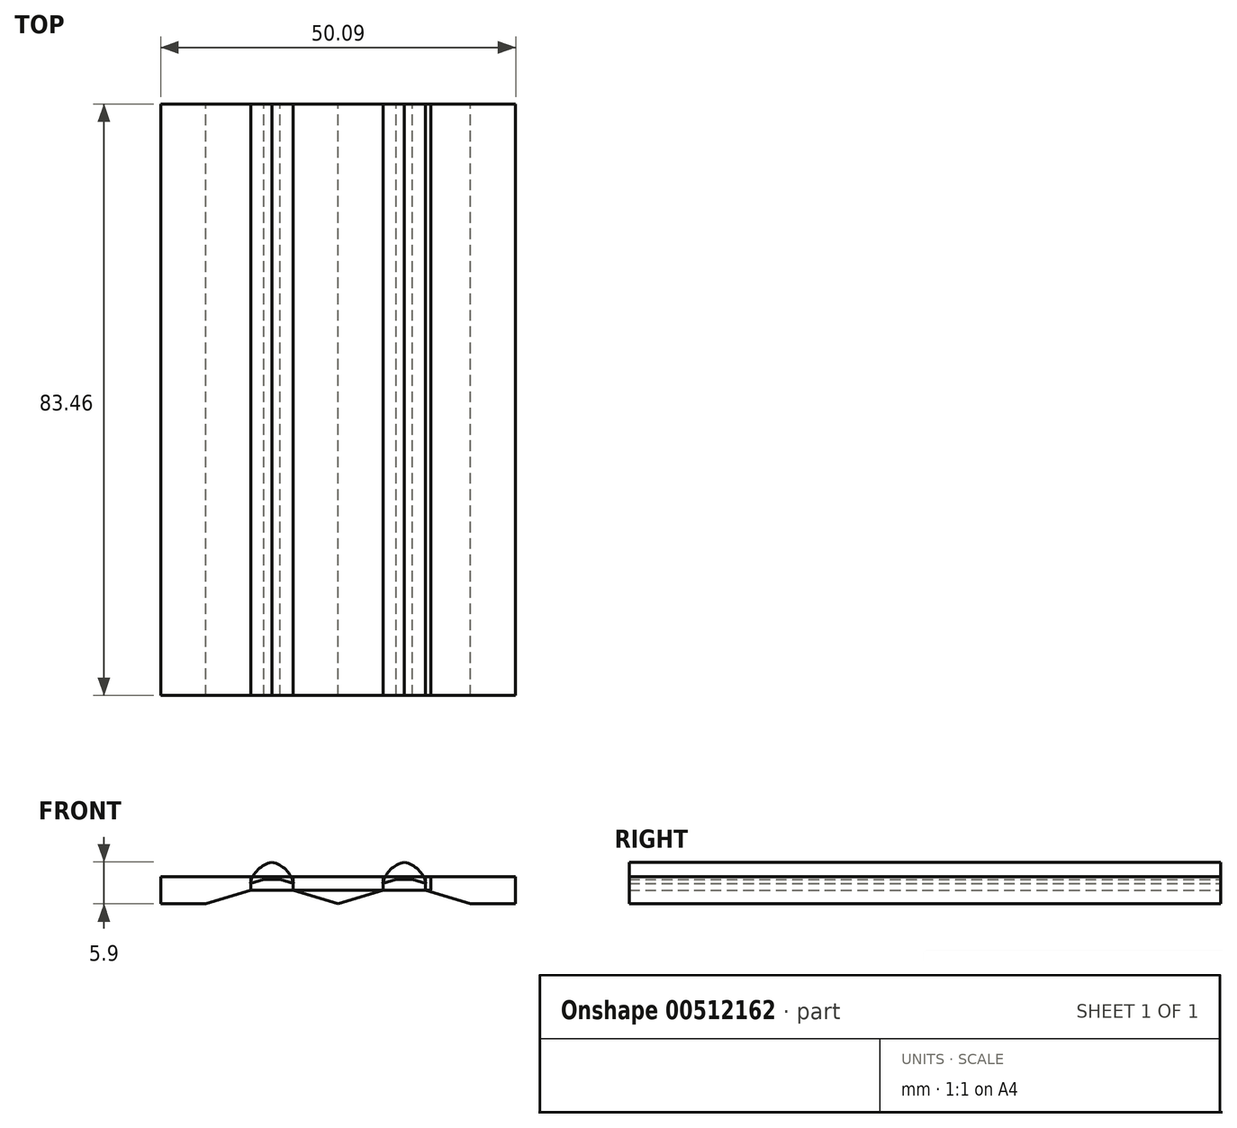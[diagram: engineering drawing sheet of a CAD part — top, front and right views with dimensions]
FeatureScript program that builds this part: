
annotation { "Feature Type Name" : "Feature", "Feature Type Description" : "" }
export const myFeature = defineFeature(function(context is Context, id is Id, definition is map)
    precondition{}
    {
        {
            var Q0;
            Q0=qCreatedBy(makeId("Top.planeOp"),FACE);
            var sketch = newSketch(context, id + "F0", { "sketchPlane" : qUnion([Q0])});
            skLineSegment(sketch, "E0.bottom", {"start": v(-28.3, 40) * mm, "end": v(22.5, 40) * mm});
            skLineSegment(sketch, "E0.top", {"start": v(-28.3, -43.46) * mm, "end": v(22.5, -43.46) * mm});
            skLineSegment(sketch, "E0.left", {"start": v(-28.3, 40) * mm, "end": v(-28.3, -43.46) * mm});
            skLineSegment(sketch, "E0.right", {"start": v(22.5, 40) * mm, "end": v(22.5, -43.46) * mm});
            skLineSegment(sketch, "E1", {"start": v(-15.6, 40) * mm, "end": v(-15.6, -43.46) * mm});
            skLineSegment(sketch, "E2", {"start": v(-15.6, -43.46) * mm, "end": v(-9.26, -43.46) * mm});
            skLineSegment(sketch, "E3", {"start": v(-9.26, -43.46) * mm, "end": v(-9.26, 40) * mm});
            skLineSegment(sketch, "E4", {"start": v(-9.26, 40) * mm, "end": v(3.44, 40) * mm});
            skLineSegment(sketch, "E5", {"start": v(3.44, 40) * mm, "end": v(3.44, -43.46) * mm});
            skLineSegment(sketch, "E6", {"start": v(3.44, -43.46) * mm, "end": v(9.8, -43.46) * mm});
            skLineSegment(sketch, "E7", {"start": v(9.8, -43.46) * mm, "end": v(9.8, 40) * mm});
            skSolve(sketch);
        }
        {
            var Q0;
            {var subQ0=sQuery(id+"F0.wireOp",EDGE,"E0.right");Q0=makeQuery(id+"F0.imprint","IMPRINT",FACE,{"disambiguationData":[TD([[makeQuery(id+"F0.imprint","IMPRINT",EDGE,{"derivedFrom":subQ0}),-1.0]])]});}
            var Q1;
            {var subQ0=sQuery(id+"F0.wireOp",EDGE,"E3");Q1=makeQuery(id+"F0.imprint","IMPRINT",FACE,{"disambiguationData":[TD([[makeQuery(id+"F0.imprint","IMPRINT",EDGE,{"derivedFrom":subQ0}),-1.0]])]});}
            var Q2;
            {var subQ0=sQuery(id+"F0.wireOp",EDGE,"E0.left");Q2=makeQuery(id+"F0.imprint","IMPRINT",FACE,{"disambiguationData":[TD([[makeQuery(id+"F0.imprint","IMPRINT",EDGE,{"derivedFrom":subQ0}),1.0]])]});}
            extrude(context, id + "F1", {"entities" : qUnion([Q0, Q1, Q2]), "depth" : 10.16 * mm});
        }
        {
            var Q0;
            {var subQ0=sQuery(id+"F0.wireOp",EDGE,"E1");Q0=makeQuery(id+"F0.imprint","IMPRINT",FACE,{"disambiguationData":[TD([[makeQuery(id+"F0.imprint","IMPRINT",EDGE,{"derivedFrom":subQ0}),1.0]])]});}
            var Q1;
            {var subQ0=sQuery(id+"F0.wireOp",EDGE,"E5");Q1=makeQuery(id+"F0.imprint","IMPRINT",FACE,{"disambiguationData":[TD([[makeQuery(id+"F0.imprint","IMPRINT",EDGE,{"derivedFrom":subQ0}),1.0]])]});}
            extrude(context, id + "F2", {"entities" : qUnion([Q0, Q1]), "depth" : 11.43 * mm});
        }
        {
            var Q0;
            Q0=makeQuery(id+"F2.opExtrude","CAP_EDGE",EDGE,{"disambiguationData":[OSD([sQuery(id+"F0.wireOp",EDGE,"E7")])],"isStart":false});
            var Q1;
            Q1=makeQuery(id+"F2.opExtrude","CAP_EDGE",EDGE,{"disambiguationData":[OSD([sQuery(id+"F0.wireOp",EDGE,"E5")])],"isStart":false});
            fillet(context, id + "F3", {"entities" : qUnion([Q0, Q1]), "radius" : 4.06 * mm, "tangentPropagation" : true, "allowEdgeOverflow" : false});
        }
        {
            var Q0;
            Q0=makeQuery(id+"F2.opExtrude","CAP_EDGE",EDGE,{"disambiguationData":[OSD([sQuery(id+"F0.wireOp",EDGE,"E3")])],"isStart":false});
            var Q1;
            Q1=makeQuery(id+"F2.opExtrude","CAP_EDGE",EDGE,{"disambiguationData":[OSD([sQuery(id+"F0.wireOp",EDGE,"E1")])],"isStart":false});
            fillet(context, id + "F4", {"entities" : qUnion([Q0, Q1]), "radius" : 4.06 * mm, "tangentPropagation" : true, "allowEdgeOverflow" : false});
        }
        {
            var Q0;
            Q0 = qSketchRegion(id + "F0", true);
            extrude(context, id + "F5", {"entities" : qUnion([Q0]), "depth" : 6.35 * mm});
        }
        {
            var Q0;
            Q0=makeQuery(id+"F5.opExtrude","SWEPT_BODY",BODY,{"disambiguationData":[OSD([sQuery(id+"F0.wireOp",EDGE,"E0.bottom"),sQuery(id+"F0.wireOp",EDGE,"E0.top"),sQuery(id+"F0.wireOp",EDGE,"E0.left"),sQuery(id+"F0.wireOp",EDGE,"E0.right"),sQuery(id+"F0.wireOp",EDGE,"E2"),sQuery(id+"F0.wireOp",EDGE,"E4"),sQuery(id+"F0.wireOp",EDGE,"E6")])]});
            var Q1;
            Q1=makeQuery(id+"F1.opExtrude","SWEPT_BODY",BODY,{"disambiguationData":[OSD([sQuery(id+"F0.wireOp",EDGE,"E0.bottom"),sQuery(id+"F0.wireOp",EDGE,"E0.top"),sQuery(id+"F0.wireOp",EDGE,"E0.right"),sQuery(id+"F0.wireOp",EDGE,"E7")])]});
            var Q2;
            Q2=makeQuery(id+"F2.opExtrude","SWEPT_BODY",BODY,{"disambiguationData":[OSD([sQuery(id+"F0.wireOp",EDGE,"E0.bottom"),sQuery(id+"F0.wireOp",EDGE,"E5"),sQuery(id+"F0.wireOp",EDGE,"E6"),sQuery(id+"F0.wireOp",EDGE,"E7")])]});
            var Q3;
            Q3=makeQuery(id+"F1.opExtrude","SWEPT_BODY",BODY,{"disambiguationData":[OSD([sQuery(id+"F0.wireOp",EDGE,"E0.top"),sQuery(id+"F0.wireOp",EDGE,"E3"),sQuery(id+"F0.wireOp",EDGE,"E4"),sQuery(id+"F0.wireOp",EDGE,"E5")])]});
            var Q4;
            Q4=makeQuery(id+"F2.opExtrude","SWEPT_BODY",BODY,{"disambiguationData":[OSD([sQuery(id+"F0.wireOp",EDGE,"E0.bottom"),sQuery(id+"F0.wireOp",EDGE,"E1"),sQuery(id+"F0.wireOp",EDGE,"E2"),sQuery(id+"F0.wireOp",EDGE,"E3")])]});
            var Q5;
            Q5=makeQuery(id+"F1.opExtrude","SWEPT_BODY",BODY,{"disambiguationData":[OSD([sQuery(id+"F0.wireOp",EDGE,"E0.bottom"),sQuery(id+"F0.wireOp",EDGE,"E0.top"),sQuery(id+"F0.wireOp",EDGE,"E0.left"),sQuery(id+"F0.wireOp",EDGE,"E1")])]});
            booleanBodies(context, id + "F6", {"operationType" : BooleanOperationType.SUBTRACTION, "tools" : qUnion([Q0]), "targets" : qUnion([Q1, Q2, Q3, Q4, Q5])});
        }
        {
            var Q0;
            Q0=qCreatedBy(makeId("Front.planeOp"),FACE);
            var sketch = newSketch(context, id + "F7", { "sketchPlane" : qUnion([Q0])});
            skLineSegment(sketch, "E8", {"start": v(-11.3, 8.9) * mm, "end": v(-2.9, 6.35) * mm});
            skLineSegment(sketch, "E9", {"start": v(-2.9, 6.35) * mm, "end": v(5.47, 8.9) * mm});
            skLineSegment(sketch, "E10", {"start": v(-13.58, 8.9) * mm, "end": v(-21.96, 6.35) * mm});
            skLineSegment(sketch, "E11", {"start": v(7.76, 8.9) * mm, "end": v(16.14, 6.35) * mm});
            skLineSegment(sketch, "E12", {"start": v(-21.96, 6.35) * mm, "end": v(16.14, 6.35) * mm});
            skLineSegment(sketch, "E13", {"start": v(-13.58, 8.9) * mm, "end": v(-11.3, 8.9) * mm});
            skLineSegment(sketch, "E14", {"start": v(5.47, 8.9) * mm, "end": v(7.76, 8.9) * mm});
            skSolve(sketch);
        }
        {
            var Q0;
            Q0 = qSketchRegion(id + "F7", true);
            extrude(context, id + "F8", {"entities" : qUnion([Q0]), "endBound" : BoundingType.SYMMETRIC, "depth" : 108.7 * mm});
        }
        {
            var Q0;
            Q0=makeQuery(id+"F8.opExtrude","SWEPT_BODY",BODY,{"disambiguationData":[OSD([sQuery(id+"F7.wireOp",EDGE,"E9"),sQuery(id+"F7.wireOp",EDGE,"E11"),sQuery(id+"F7.wireOp",EDGE,"E12"),sQuery(id+"F7.wireOp",EDGE,"E14")])]});
            var Q1;
            Q1=makeQuery(id+"F8.opExtrude","SWEPT_BODY",BODY,{"disambiguationData":[OSD([sQuery(id+"F7.wireOp",EDGE,"E8"),sQuery(id+"F7.wireOp",EDGE,"E10"),sQuery(id+"F7.wireOp",EDGE,"E12"),sQuery(id+"F7.wireOp",EDGE,"E13")])]});
            var Q2;
            Q2=makeQuery(id+"F1.opExtrude","SWEPT_BODY",BODY,{"disambiguationData":[OSD([sQuery(id+"F0.wireOp",EDGE,"E0.bottom"),sQuery(id+"F0.wireOp",EDGE,"E0.top"),sQuery(id+"F0.wireOp",EDGE,"E0.right"),sQuery(id+"F0.wireOp",EDGE,"E7")])]});
            var Q3;
            Q3=makeQuery(id+"F2.opExtrude","SWEPT_BODY",BODY,{"disambiguationData":[OSD([sQuery(id+"F0.wireOp",EDGE,"E0.bottom"),sQuery(id+"F0.wireOp",EDGE,"E5"),sQuery(id+"F0.wireOp",EDGE,"E6"),sQuery(id+"F0.wireOp",EDGE,"E7")])]});
            var Q4;
            Q4=makeQuery(id+"F1.opExtrude","SWEPT_BODY",BODY,{"disambiguationData":[OSD([sQuery(id+"F0.wireOp",EDGE,"E0.top"),sQuery(id+"F0.wireOp",EDGE,"E3"),sQuery(id+"F0.wireOp",EDGE,"E4"),sQuery(id+"F0.wireOp",EDGE,"E5")])]});
            var Q5;
            Q5=makeQuery(id+"F2.opExtrude","SWEPT_BODY",BODY,{"disambiguationData":[OSD([sQuery(id+"F0.wireOp",EDGE,"E0.bottom"),sQuery(id+"F0.wireOp",EDGE,"E1"),sQuery(id+"F0.wireOp",EDGE,"E2"),sQuery(id+"F0.wireOp",EDGE,"E3")])]});
            var Q6;
            Q6=makeQuery(id+"F1.opExtrude","SWEPT_BODY",BODY,{"disambiguationData":[OSD([sQuery(id+"F0.wireOp",EDGE,"E0.bottom"),sQuery(id+"F0.wireOp",EDGE,"E0.top"),sQuery(id+"F0.wireOp",EDGE,"E0.left"),sQuery(id+"F0.wireOp",EDGE,"E1")])]});
            booleanBodies(context, id + "F9", {"operationType" : BooleanOperationType.SUBTRACTION, "tools" : qUnion([Q0, Q1]), "targets" : qUnion([Q2, Q3, Q4, Q5, Q6])});
        }
        {
            var Q0;
            Q0=makeQuery(id+"F1.opExtrude","SWEPT_BODY",BODY,{"disambiguationData":[OSD([sQuery(id+"F0.wireOp",EDGE,"E0.bottom"),sQuery(id+"F0.wireOp",EDGE,"E0.top"),sQuery(id+"F0.wireOp",EDGE,"E0.right"),sQuery(id+"F0.wireOp",EDGE,"E7")])]});
            var Q1;
            Q1=makeQuery(id+"F1.opExtrude","SWEPT_BODY",BODY,{"disambiguationData":[OSD([sQuery(id+"F0.wireOp",EDGE,"E0.bottom"),sQuery(id+"F0.wireOp",EDGE,"E0.top"),sQuery(id+"F0.wireOp",EDGE,"E0.left"),sQuery(id+"F0.wireOp",EDGE,"E1")])]});
            var Q2;
            Q2=makeQuery(id+"F1.opExtrude","SWEPT_BODY",BODY,{"disambiguationData":[OSD([sQuery(id+"F0.wireOp",EDGE,"E0.top"),sQuery(id+"F0.wireOp",EDGE,"E3"),sQuery(id+"F0.wireOp",EDGE,"E4"),sQuery(id+"F0.wireOp",EDGE,"E5")])]});
            var Q3;
            Q3=makeQuery(id+"F2.opExtrude","SWEPT_BODY",BODY,{"disambiguationData":[OSD([sQuery(id+"F0.wireOp",EDGE,"E0.bottom"),sQuery(id+"F0.wireOp",EDGE,"E1"),sQuery(id+"F0.wireOp",EDGE,"E2"),sQuery(id+"F0.wireOp",EDGE,"E3")])]});
            var Q4;
            Q4=makeQuery(id+"F2.opExtrude","SWEPT_BODY",BODY,{"disambiguationData":[OSD([sQuery(id+"F0.wireOp",EDGE,"E0.bottom"),sQuery(id+"F0.wireOp",EDGE,"E5"),sQuery(id+"F0.wireOp",EDGE,"E6"),sQuery(id+"F0.wireOp",EDGE,"E7")])]});
            transform(context, id + "F10", {"entities" : qUnion([Q0, Q1, Q2, Q3, Q4]), "transformType" : TransformType.TRANSLATION_3D, "dx" : 2.54 * mm, "dy" : 0 * mm, "dz" : 0 * mm, "makeCopy" : false});
        }
        {
            var Q0;
            Q0=makeQuery(id+"F1.opExtrude","SWEPT_BODY",BODY,{"disambiguationData":[OSD([sQuery(id+"F0.wireOp",EDGE,"E0.bottom"),sQuery(id+"F0.wireOp",EDGE,"E0.top"),sQuery(id+"F0.wireOp",EDGE,"E0.right"),sQuery(id+"F0.wireOp",EDGE,"E7")])]});
            var Q1;
            Q1=makeQuery(id+"F1.opExtrude","SWEPT_BODY",BODY,{"disambiguationData":[OSD([sQuery(id+"F0.wireOp",EDGE,"E0.bottom"),sQuery(id+"F0.wireOp",EDGE,"E0.top"),sQuery(id+"F0.wireOp",EDGE,"E0.left"),sQuery(id+"F0.wireOp",EDGE,"E1")])]});
            var Q2;
            Q2=makeQuery(id+"F1.opExtrude","SWEPT_BODY",BODY,{"disambiguationData":[OSD([sQuery(id+"F0.wireOp",EDGE,"E0.top"),sQuery(id+"F0.wireOp",EDGE,"E3"),sQuery(id+"F0.wireOp",EDGE,"E4"),sQuery(id+"F0.wireOp",EDGE,"E5")])]});
            var Q3;
            Q3=makeQuery(id+"F2.opExtrude","SWEPT_BODY",BODY,{"disambiguationData":[OSD([sQuery(id+"F0.wireOp",EDGE,"E0.bottom"),sQuery(id+"F0.wireOp",EDGE,"E1"),sQuery(id+"F0.wireOp",EDGE,"E2"),sQuery(id+"F0.wireOp",EDGE,"E3")])]});
            var Q4;
            Q4=makeQuery(id+"F2.opExtrude","SWEPT_BODY",BODY,{"disambiguationData":[OSD([sQuery(id+"F0.wireOp",EDGE,"E0.bottom"),sQuery(id+"F0.wireOp",EDGE,"E5"),sQuery(id+"F0.wireOp",EDGE,"E6"),sQuery(id+"F0.wireOp",EDGE,"E7")])]});
            transform(context, id + "F11", {"entities" : qUnion([Q0, Q1, Q2, Q3, Q4]), "transformType" : TransformType.TRANSLATION_3D, "dx" : 0.25 * mm, "dy" : 0 * mm, "dz" : 0 * mm, "makeCopy" : false});
        }
        {
            var Q0;
            Q0=makeQuery(id+"F2.opExtrude","SWEPT_BODY",BODY,{"disambiguationData":[OSD([sQuery(id+"F0.wireOp",EDGE,"E0.bottom"),sQuery(id+"F0.wireOp",EDGE,"E1"),sQuery(id+"F0.wireOp",EDGE,"E2"),sQuery(id+"F0.wireOp",EDGE,"E3")])]});
            transform(context, id + "F12", {"entities" : qUnion([Q0]), "transformType" : TransformType.TRANSLATION_3D, "dx" : 0 * mm, "dy" : 0 * mm, "dz" : 0.91 * mm, "makeCopy" : false});
        }
        {
            var Q0;
            Q0=makeQuery(id+"F1.opExtrude","SWEPT_BODY",BODY,{"disambiguationData":[OSD([sQuery(id+"F0.wireOp",EDGE,"E0.bottom"),sQuery(id+"F0.wireOp",EDGE,"E0.top"),sQuery(id+"F0.wireOp",EDGE,"E0.left"),sQuery(id+"F0.wireOp",EDGE,"E1")])]});
            transform(context, id + "F13", {"entities" : qUnion([Q0]), "transformType" : TransformType.TRANSLATION_3D, "dx" : 0.18 * mm, "dy" : 0 * mm, "dz" : 0 * mm, "makeCopy" : false});
        }
        {
            var Q0;
            Q0=makeQuery(id+"F1.opExtrude","SWEPT_BODY",BODY,{"disambiguationData":[OSD([sQuery(id+"F0.wireOp",EDGE,"E0.bottom"),sQuery(id+"F0.wireOp",EDGE,"E0.top"),sQuery(id+"F0.wireOp",EDGE,"E0.left"),sQuery(id+"F0.wireOp",EDGE,"E1")])]});
            var Q1;
            Q1=makeQuery(id+"F2.opExtrude","SWEPT_BODY",BODY,{"disambiguationData":[OSD([sQuery(id+"F0.wireOp",EDGE,"E0.bottom"),sQuery(id+"F0.wireOp",EDGE,"E1"),sQuery(id+"F0.wireOp",EDGE,"E2"),sQuery(id+"F0.wireOp",EDGE,"E3")])]});
            transform(context, id + "F14", {"entities" : qUnion([Q0, Q1]), "transformType" : TransformType.TRANSLATION_3D, "dx" : 0.18 * mm, "dy" : 0 * mm, "dz" : 0 * mm, "makeCopy" : false});
        }
        {
            var Q0;
            Q0=makeQuery(id+"F2.opExtrude","SWEPT_BODY",BODY,{"disambiguationData":[OSD([sQuery(id+"F0.wireOp",EDGE,"E0.bottom"),sQuery(id+"F0.wireOp",EDGE,"E5"),sQuery(id+"F0.wireOp",EDGE,"E6"),sQuery(id+"F0.wireOp",EDGE,"E7")])]});
            transform(context, id + "F15", {"entities" : qUnion([Q0]), "transformType" : TransformType.TRANSLATION_3D, "dx" : 0 * mm, "dy" : 0 * mm, "dz" : 0.91 * mm, "makeCopy" : false});
        }
        {
            var Q0;
            Q0=makeQuery(id+"F1.opExtrude","SWEPT_BODY",BODY,{"disambiguationData":[OSD([sQuery(id+"F0.wireOp",EDGE,"E0.top"),sQuery(id+"F0.wireOp",EDGE,"E3"),sQuery(id+"F0.wireOp",EDGE,"E4"),sQuery(id+"F0.wireOp",EDGE,"E5")])]});
            var Q1;
            Q1=makeQuery(id+"F2.opExtrude","SWEPT_BODY",BODY,{"disambiguationData":[OSD([sQuery(id+"F0.wireOp",EDGE,"E0.bottom"),sQuery(id+"F0.wireOp",EDGE,"E1"),sQuery(id+"F0.wireOp",EDGE,"E2"),sQuery(id+"F0.wireOp",EDGE,"E3")])]});
            var Q2;
            Q2=makeQuery(id+"F1.opExtrude","SWEPT_BODY",BODY,{"disambiguationData":[OSD([sQuery(id+"F0.wireOp",EDGE,"E0.bottom"),sQuery(id+"F0.wireOp",EDGE,"E0.top"),sQuery(id+"F0.wireOp",EDGE,"E0.left"),sQuery(id+"F0.wireOp",EDGE,"E1")])]});
            transform(context, id + "F16", {"entities" : qUnion([Q0, Q1, Q2]), "transformType" : TransformType.TRANSLATION_3D, "dx" : 0.18 * mm, "dy" : 0 * mm, "dz" : 0 * mm, "makeCopy" : false});
        }
        {
            var Q0;
            Q0=makeQuery(id+"F1.opExtrude","SWEPT_BODY",BODY,{"disambiguationData":[OSD([sQuery(id+"F0.wireOp",EDGE,"E0.bottom"),sQuery(id+"F0.wireOp",EDGE,"E0.top"),sQuery(id+"F0.wireOp",EDGE,"E0.left"),sQuery(id+"F0.wireOp",EDGE,"E1")])]});
            var Q1;
            Q1=makeQuery(id+"F2.opExtrude","SWEPT_BODY",BODY,{"disambiguationData":[OSD([sQuery(id+"F0.wireOp",EDGE,"E0.bottom"),sQuery(id+"F0.wireOp",EDGE,"E1"),sQuery(id+"F0.wireOp",EDGE,"E2"),sQuery(id+"F0.wireOp",EDGE,"E3")])]});
            var Q2;
            Q2=makeQuery(id+"F1.opExtrude","SWEPT_BODY",BODY,{"disambiguationData":[OSD([sQuery(id+"F0.wireOp",EDGE,"E0.top"),sQuery(id+"F0.wireOp",EDGE,"E3"),sQuery(id+"F0.wireOp",EDGE,"E4"),sQuery(id+"F0.wireOp",EDGE,"E5")])]});
            var Q3;
            Q3=makeQuery(id+"F2.opExtrude","SWEPT_BODY",BODY,{"disambiguationData":[OSD([sQuery(id+"F0.wireOp",EDGE,"E0.bottom"),sQuery(id+"F0.wireOp",EDGE,"E5"),sQuery(id+"F0.wireOp",EDGE,"E6"),sQuery(id+"F0.wireOp",EDGE,"E7")])]});
            transform(context, id + "F17", {"entities" : qUnion([Q0, Q1, Q2, Q3]), "transformType" : TransformType.TRANSLATION_3D, "dx" : 0.18 * mm, "dy" : 0 * mm, "dz" : 0 * mm, "makeCopy" : false});
        }
        {
            var Q0;
            Q0=makeQuery(id+"F1.opExtrude","SWEPT_FACE",FACE,{"disambiguationData":[OSD([sQuery(id+"F0.wireOp",EDGE,"E1")])]});
            extrude(context, id + "F18", {"entities" : qUnion([Q0]), "depth" : 25.4 * mm});
        }
    });
